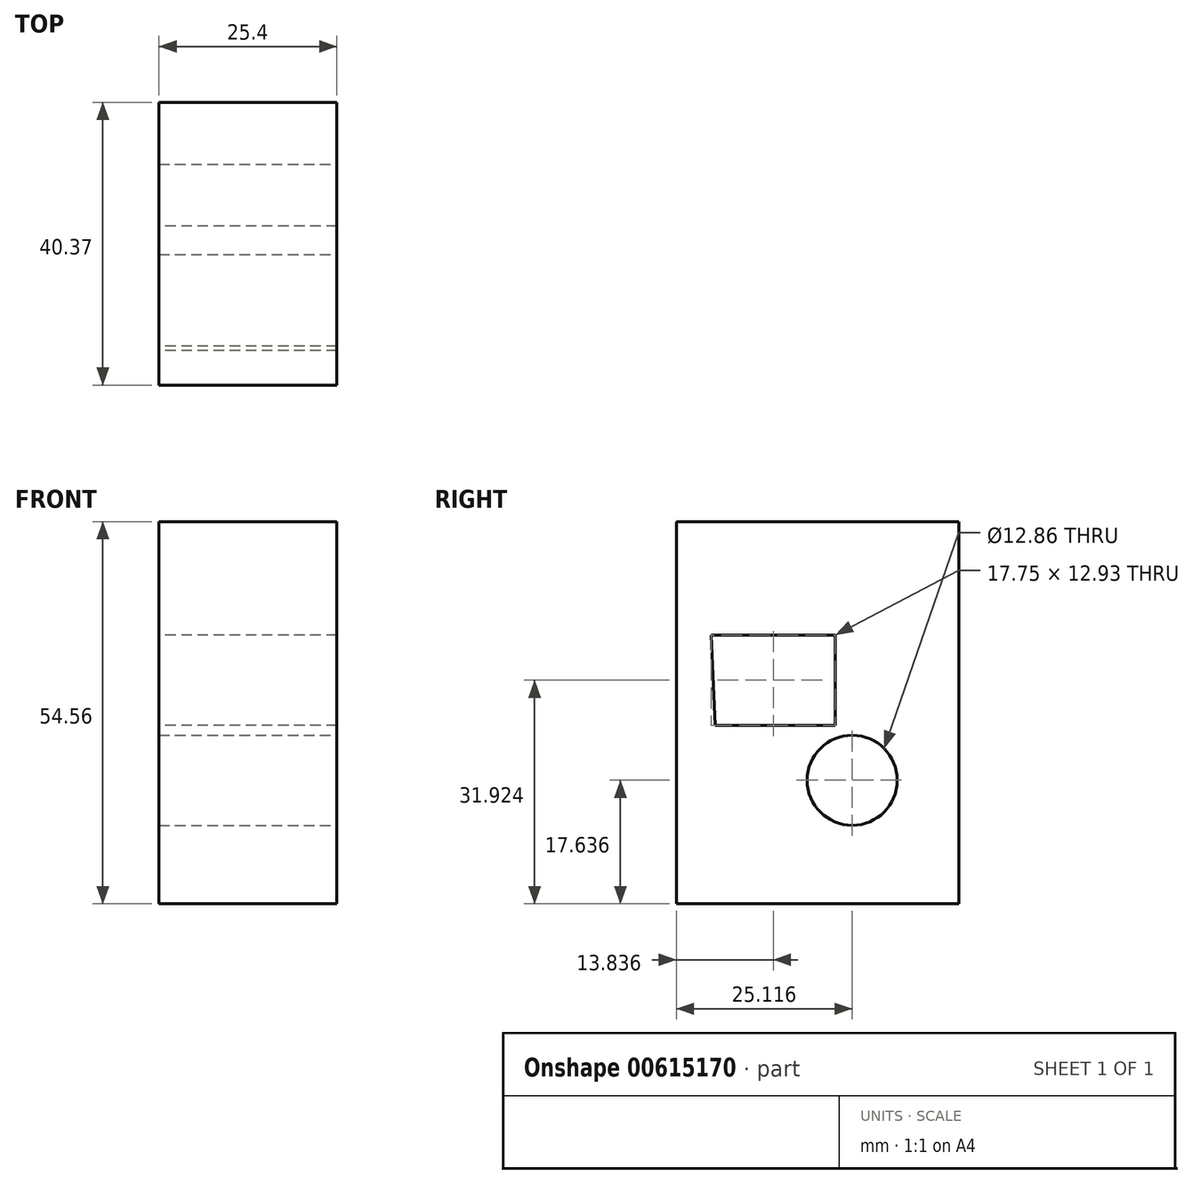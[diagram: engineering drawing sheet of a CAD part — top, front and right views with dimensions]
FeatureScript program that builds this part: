
annotation { "Feature Type Name" : "Feature", "Feature Type Description" : "" }
export const myFeature = defineFeature(function(context is Context, id is Id, definition is map)
    precondition{}
    {
        {
            var Q0;
            Q0=qCreatedBy(makeId("Right.planeOp"),FACE);
            var sketch = newSketch(context, id + "F0", { "sketchPlane" : qUnion([Q0])});
            skLineSegment(sketch, "E0.bottom", {"start": v(0, -2.63) * mm, "end": v(40.37, -2.63) * mm});
            skLineSegment(sketch, "E0.top", {"start": v(0, -57.19) * mm, "end": v(40.37, -57.19) * mm});
            skLineSegment(sketch, "E0.left", {"start": v(0, -2.63) * mm, "end": v(0, -57.19) * mm});
            skLineSegment(sketch, "E0.right", {"start": v(40.37, -2.63) * mm, "end": v(40.37, -57.19) * mm});
            skLineSegment(sketch, "E1", {"start": v(5.56, -31.73) * mm, "end": v(22.7, -31.73) * mm});
            skLineSegment(sketch, "E2", {"start": v(22.7, -31.73) * mm, "end": v(22.7, -18.8) * mm});
            skLineSegment(sketch, "E3", {"start": v(22.7, -18.8) * mm, "end": v(4.96, -18.8) * mm});
            skLineSegment(sketch, "E4", {"start": v(4.96, -18.8) * mm, "end": v(5.56, -31.73) * mm});
            skSolve(sketch);
        }
        {
            var Q0;
            Q0 = qSketchRegion(id + "F0", true);
            extrude(context, id + "F1", {"entities" : qUnion([Q0]), "depth" : 25.4 * mm, "offsetDistance" : 25.4 * mm});
        }
        {
            var Q0;
            Q0=makeQuery(id+"F1.opExtrude","CAP_FACE",FACE,{"disambiguationData":[OSD([sQuery(id+"F0.wireOp",EDGE,"E0.bottom"),sQuery(id+"F0.wireOp",EDGE,"E0.top"),sQuery(id+"F0.wireOp",EDGE,"E0.left"),sQuery(id+"F0.wireOp",EDGE,"E0.right"),sQuery(id+"F0.wireOp",EDGE,"E1"),sQuery(id+"F0.wireOp",EDGE,"E2"),sQuery(id+"F0.wireOp",EDGE,"E3"),sQuery(id+"F0.wireOp",EDGE,"E4")])],"isStart":false});
            var sketch = newSketch(context, id + "F2", { "sketchPlane" : qUnion([Q0])});
            skCircle(sketch, "E5", {"center": v(25.12, -39.55) * mm, "radius": 6.43 * mm});
            skSolve(sketch);
        }
        {
            var Q0;
            Q0=makeQuery(id+"F2.imprint","IMPRINT",FACE,{"disambiguationData":[TD([[makeQuery(id+"F2.imprint","IMPRINT",EDGE,{"derivedFrom":sQuery(id+"F2.wireOp",EDGE,"E5")}),1.0]])]});
            extrude(context, id + "F3", {"entities" : qUnion([Q0]), "operationType" : NewBodyOperationType.REMOVE, "endBound" : BoundingType.THROUGH_ALL, "oppositeDirection" : true, "depth" : 94.74 * mm, "offsetDistance" : 25.4 * mm});
        }
    });
